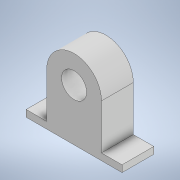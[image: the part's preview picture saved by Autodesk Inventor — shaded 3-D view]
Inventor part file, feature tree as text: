
AUTODESK INVENTOR PART (.ipt)
format: ipt  version: 2021 (Build 250183000, 183)  size: 106,496 bytes
history: native  units: mm
features: other x1, extrude x1, sketch x1
ambient origin geometry x8: Origin, YZ Plane, XZ Plane, XY Plane, X Axis, Y Axis, Z Axis, Center Point
bodies: Body1 (feature_tree)
feature tree (3):
  other  "Sólido1"
  extrude  "Extrusión1"  [1 undecoded]
  sketch  "Boceto1"  dims[d0=10.0mm d1=0.0mm]
note: 1 required parameter value undecoded (feature->parameter linkage not recoverable at this tier; creation-order binding heuristic only, values carry confidence <= 0.55)
